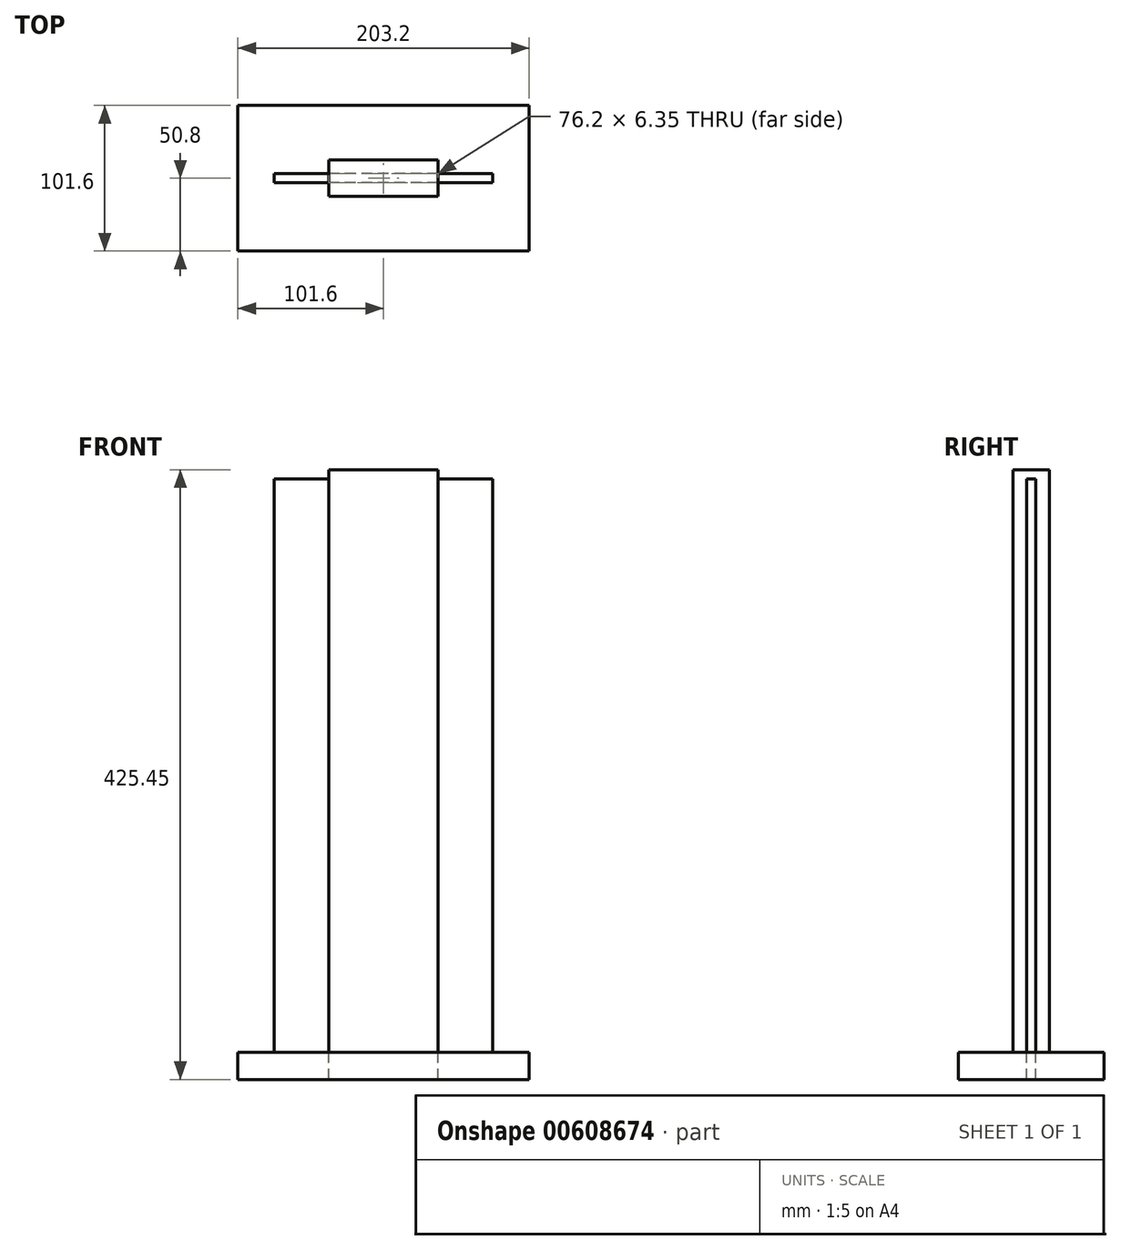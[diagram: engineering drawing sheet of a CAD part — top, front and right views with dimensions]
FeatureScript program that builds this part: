
annotation { "Feature Type Name" : "Feature", "Feature Type Description" : "" }
export const myFeature = defineFeature(function(context is Context, id is Id, definition is map)
    precondition{}
    {
        {
            var Q0;
            Q0=qCreatedBy(makeId("Top.planeOp"),FACE);
            var sketch = newSketch(context, id + "F0", { "sketchPlane" : qUnion([Q0])});
            skLineSegment(sketch, "E0.bottom", {"start": v(-101.6, 50.8) * mm, "end": v(101.6, 50.8) * mm});
            skLineSegment(sketch, "E0.top", {"start": v(-101.6, -50.8) * mm, "end": v(101.6, -50.8) * mm});
            skLineSegment(sketch, "E0.left", {"start": v(-101.6, 50.8) * mm, "end": v(-101.6, -50.8) * mm});
            skLineSegment(sketch, "E0.right", {"start": v(101.6, 50.8) * mm, "end": v(101.6, -50.8) * mm});
            skPoint(sketch, "E0.middle", {"position": v(0, 0) * mm});
            skLineSegment(sketch, "E1.bottom", {"start": v(38.1, 12.7) * mm, "end": v(-38.1, 12.7) * mm});
            skLineSegment(sketch, "E1.top", {"start": v(38.1, -12.7) * mm, "end": v(-38.1, -12.7) * mm});
            skLineSegment(sketch, "E1.left", {"start": v(38.1, 12.7) * mm, "end": v(38.1, -12.7) * mm});
            skLineSegment(sketch, "E1.right", {"start": v(-38.1, 12.7) * mm, "end": v(-38.1, -12.7) * mm});
            skLineSegment(sketch, "E2.bottom", {"start": v(38.1, 3.17) * mm, "end": v(76.2, 3.17) * mm});
            skLineSegment(sketch, "E2.top", {"start": v(38.1, -3.18) * mm, "end": v(76.2, -3.18) * mm});
            skLineSegment(sketch, "E2.left", {"start": v(38.1, 3.17) * mm, "end": v(38.1, -3.18) * mm});
            skLineSegment(sketch, "E2.right", {"start": v(76.2, 3.18) * mm, "end": v(76.2, -3.17) * mm});
            skPoint(sketch, "E2.middle", {"position": v(57.15, 0) * mm});
            skLineSegment(sketch, "E3.bottom", {"start": v(38.1, 3.17) * mm, "end": v(-76.2, 3.17) * mm});
            skLineSegment(sketch, "E3.top", {"start": v(38.1, -3.18) * mm, "end": v(-76.2, -3.18) * mm});
            skLineSegment(sketch, "E3.right", {"start": v(-76.2, 3.17) * mm, "end": v(-76.2, -3.18) * mm});
            skSolve(sketch);
        }
        {
            var Q0;
            Q0=makeQuery(id+"F0.imprint","IMPRINT",FACE,{"disambiguationData":[TD([[makeQuery(id+"F0.imprint","IMPRINT",EDGE,{"derivedFrom":sQuery(id+"F0.wireOp",EDGE,"E0.bottom")}),-1.0]])]});
            var Q1;
            {var subQ3=sQuery(id+"F0.wireOp",EDGE,"E1.bottom");Q1=makeQuery(id+"F0.imprint","IMPRINT",FACE,{"disambiguationData":[TD([[makeQuery(id+"F0.imprint","IMPRINT",EDGE,{"derivedFrom":subQ3}),1.0]])]});}
            var Q2;
            Q2=makeQuery(id+"F0.imprint","IMPRINT",FACE,{"disambiguationData":[TD([[makeQuery(id+"F0.imprint","IMPRINT",EDGE,{"derivedFrom":sQuery(id+"F0.wireOp",EDGE,"E2.bottom")}),-1.0]])]});
            var Q3;
            {var subQ5=sQuery(id+"F0.wireOp",EDGE,"E2.left");Q3=makeQuery(id+"F0.imprint","IMPRINT",FACE,{"disambiguationData":[TD([[makeQuery(id+"F0.imprint","IMPRINT",EDGE,{"derivedFrom":subQ5}),-1.0]])]});}
            var Q4;
            {var subQ0=sQuery(id+"F0.wireOp",EDGE,"E1.top");Q4=makeQuery(id+"F0.imprint","IMPRINT",FACE,{"disambiguationData":[TD([[makeQuery(id+"F0.imprint","IMPRINT",EDGE,{"derivedFrom":subQ0}),-1.0]])]});}
            var Q5;
            {var subQ5=sQuery(id+"F0.wireOp",EDGE,"E3.right");Q5=makeQuery(id+"F0.imprint","IMPRINT",FACE,{"disambiguationData":[TD([[makeQuery(id+"F0.imprint","IMPRINT",EDGE,{"derivedFrom":subQ5}),1.0]])]});}
            extrude(context, id + "F1", {"entities" : qUnion([Q0, Q1, Q2, Q3, Q4, Q5]), "oppositeDirection" : true, "depth" : 19.05 * mm, "offsetDistance" : 25.4 * mm});
        }
        {
            var Q0;
            {var subQ3=sQuery(id+"F0.wireOp",EDGE,"E1.bottom");Q0=makeQuery(id+"F0.imprint","IMPRINT",FACE,{"disambiguationData":[TD([[makeQuery(id+"F0.imprint","IMPRINT",EDGE,{"derivedFrom":subQ3}),1.0]])]});}
            var Q1;
            {var subQ0=sQuery(id+"F0.wireOp",EDGE,"E1.top");Q1=makeQuery(id+"F0.imprint","IMPRINT",FACE,{"disambiguationData":[TD([[makeQuery(id+"F0.imprint","IMPRINT",EDGE,{"derivedFrom":subQ0}),-1.0]])]});}
            extrude(context, id + "F2", {"entities" : qUnion([Q0, Q1]), "depth" : 406.4 * mm, "offsetDistance" : 25.4 * mm});
        }
        {
            var Q0;
            Q0=makeQuery(id+"F0.imprint","IMPRINT",FACE,{"disambiguationData":[TD([[makeQuery(id+"F0.imprint","IMPRINT",EDGE,{"derivedFrom":sQuery(id+"F0.wireOp",EDGE,"E2.bottom")}),-1.0]])]});
            var Q1;
            Q1=makeQuery(id+"F0.imprint","IMPRINT",FACE,{"disambiguationData":[TD([[makeQuery(id+"F0.imprint","IMPRINT",EDGE,{"derivedFrom":sQuery(id+"F0.wireOp",EDGE,"E3.bottom")}),1.0]])]});
            extrude(context, id + "F3", {"entities" : qUnion([Q0, Q1]), "depth" : 400.05 * mm, "offsetDistance" : 25.4 * mm});
        }
        {
            var Q0;
            Q0=makeQuery(id+"F2.opExtrude","CAP_FACE",FACE,{"disambiguationData":[OSD([sQuery(id+"F0.wireOp",EDGE,"E1.bottom"),sQuery(id+"F0.wireOp",EDGE,"E1.top"),sQuery(id+"F0.wireOp",EDGE,"E1.left"),sQuery(id+"F0.wireOp",EDGE,"E1.right"),sQuery(id+"F0.wireOp",EDGE,"E3.bottom"),sQuery(id+"F0.wireOp",EDGE,"E3.top"),sQuery(id+"F0.wireOp",EDGE,"E3.right")])],"isStart":false});
            var sketch = newSketch(context, id + "F4", { "sketchPlane" : qUnion([Q0])});
            skLineSegment(sketch, "E4.0.0", {"start": v(-38.1, 3.17) * mm, "end": v(38.1, 3.17) * mm});
            skLineSegment(sketch, "E4.0.1", {"start": v(38.1, 3.17) * mm, "end": v(38.1, 12.7) * mm});
            skLineSegment(sketch, "E4.0.2", {"start": v(38.1, 12.7) * mm, "end": v(-38.1, 12.7) * mm});
            skLineSegment(sketch, "E4.0.3", {"start": v(-38.1, 12.7) * mm, "end": v(-38.1, 3.17) * mm});
            skLineSegment(sketch, "E4.0.4", {"start": v(-76.2, -12.7) * mm, "end": v(38.1, -12.7) * mm});
            skLineSegment(sketch, "E4.0.5", {"start": v(38.1, -12.7) * mm, "end": v(38.1, -3.18) * mm});
            skLineSegment(sketch, "E4.0.6", {"start": v(38.1, -3.18) * mm, "end": v(-38.1, -3.18) * mm});
            skLineSegment(sketch, "E4.0.7", {"start": v(-38.1, -3.18) * mm, "end": v(-38.1, 3.17) * mm});
            skLineSegment(sketch, "E5", {"start": v(38.1, 3.17) * mm, "end": v(38.1, -3.18) * mm});
            skSolve(sketch);
        }
        {
            var Q0;
            Q0=makeQuery(id+"F4.imprint","IMPRINT",FACE,{"disambiguationData":[TD([[makeQuery(id+"F4.imprint","IMPRINT",EDGE,{"derivedFrom":sQuery(id+"F4.wireOp",EDGE,"E4.0.0")}),-1.0]])]});
            var Q1;
            Q1=makeQuery(id+"F4.imprint","IMPRINT",FACE,{"disambiguationData":[TD([[makeQuery(id+"F4.imprint","IMPRINT",EDGE,{"derivedFrom":sQuery(id+"F4.wireOp",EDGE,"E4.0.0")}),1.0]])]});
            extrude(context, id + "F5", {"entities" : qUnion([Q0, Q1]), "operationType" : NewBodyOperationType.ADD, "oppositeDirection" : true, "depth" : 6.35 * mm, "offsetDistance" : 25.4 * mm});
        }
    });
